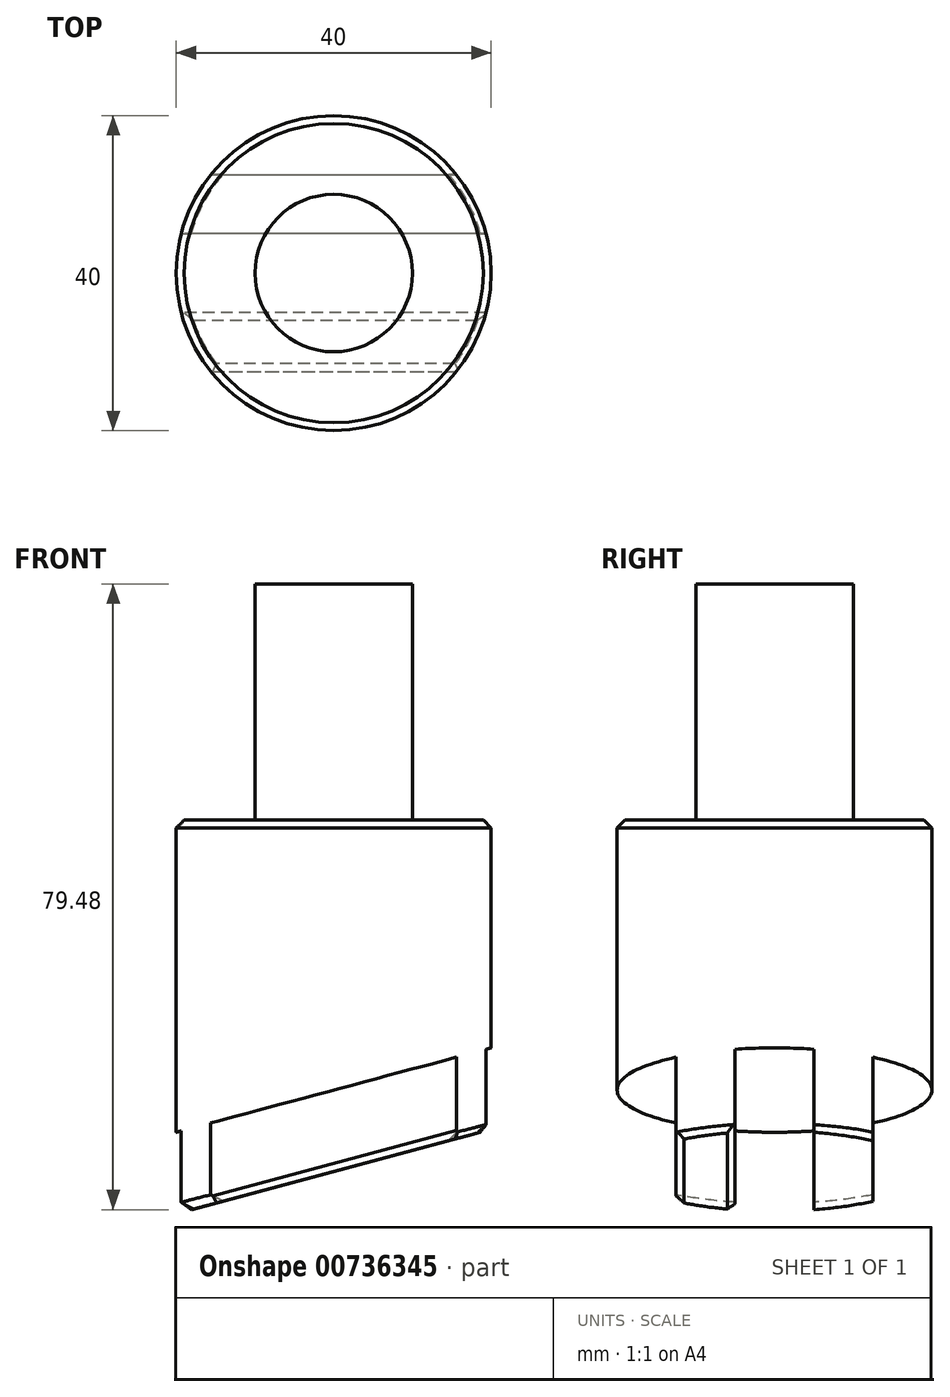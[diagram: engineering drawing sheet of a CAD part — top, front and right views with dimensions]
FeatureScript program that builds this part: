
annotation { "Feature Type Name" : "Feature", "Feature Type Description" : "" }
export const myFeature = defineFeature(function(context is Context, id is Id, definition is map)
    precondition{}
    {
        {
            var Q0;
            Q0=qCreatedBy(makeId("Front.planeOp"),FACE);
            var sketch = newSketch(context, id + "F0", { "sketchPlane" : qUnion([Q0])});
            skLineSegment(sketch, "E0", {"start": v(0, 0) * mm, "end": v(0, 80) * mm});
            skLineSegment(sketch, "E1", {"start": v(0, 80) * mm, "end": v(-10, 80) * mm});
            skLineSegment(sketch, "E2", {"start": v(-10, 80) * mm, "end": v(-10, 50) * mm});
            skLineSegment(sketch, "E3", {"start": v(-10, 50) * mm, "end": v(-20, 50) * mm});
            skLineSegment(sketch, "E4", {"start": v(-20, 50) * mm, "end": v(-20, 0) * mm});
            skLineSegment(sketch, "E5", {"start": v(-20, 0) * mm, "end": v(0, 0) * mm});
            skSolve(sketch);
        }
        {
            var Q0;
            Q0=makeQuery(id+"F0.imprint","IMPRINT",FACE,{"disambiguationData":[TD([[makeQuery(id+"F0.imprint","IMPRINT",EDGE,{"derivedFrom":sQuery(id+"F0.wireOp",EDGE,"E0")}),1.0]])]});
            var Q1;
            Q1=sQuery(id+"F0.wireOp",EDGE,"E0");
            revolve(context, id + "F1", {"surfaceOperationType" : NewSurfaceOperationType.NEW, "entities" : qUnion([Q0]), "axis" : qUnion([Q1]), "revolveType" : RevolveType.FULL});
        }
        {
            var Q0;
            Q0=qCreatedBy(makeId("Front.planeOp"),FACE);
            var sketch = newSketch(context, id + "F2", { "sketchPlane" : qUnion([Q0])});
            skLineSegment(sketch, "E6", {"start": v(-20, 0) * mm, "end": v(20, 10.72) * mm});
            skLineSegment(sketch, "E7", {"start": v(-20, 0) * mm, "end": v(20, 0) * mm});
            skLineSegment(sketch, "E8", {"start": v(20, 0) * mm, "end": v(20, 10.72) * mm});
            skSolve(sketch);
        }
        {
            var Q0;
            Q0 = qSketchRegion(id + "F2", true);
            extrude(context, id + "F3", {"entities" : qUnion([Q0]), "operationType" : NewBodyOperationType.REMOVE, "endBound" : BoundingType.SYMMETRIC, "depth" : 40 * mm, "offsetDistance" : 25 * mm});
        }
        {
            var Q0;
            Q0=makeQuery(id+"F3.boolean.opBoolean","COPY",FACE,{"derivedFrom":makeQuery(id+"F3.opExtrude","SWEPT_FACE",FACE,{"disambiguationData":[OSD([sQuery(id+"F2.wireOp",EDGE,"E6")])]})});
            var sketch = newSketch(context, id + "F4", { "sketchPlane" : qUnion([Q0])});
            skLineSegment(sketch, "E9.bottom", {"start": v(30, -5) * mm, "end": v(-30, -5) * mm});
            skLineSegment(sketch, "E9.top", {"start": v(30, 5) * mm, "end": v(-30, 5) * mm});
            skLineSegment(sketch, "E9.left", {"start": v(30, -5) * mm, "end": v(30, 5) * mm});
            skLineSegment(sketch, "E9.right", {"start": v(-30, -5) * mm, "end": v(-30, 5) * mm});
            skPoint(sketch, "E9.middle", {"position": v(0, 0) * mm});
            skLineSegment(sketch, "E10", {"start": v(-30, 12.5) * mm, "end": v(30, 12.5) * mm});
            skLineSegment(sketch, "E11", {"start": v(30, 12.5) * mm, "end": v(30, 25) * mm});
            skLineSegment(sketch, "E12", {"start": v(30, 25) * mm, "end": v(-30, 25) * mm});
            skLineSegment(sketch, "E13", {"start": v(-30, 25) * mm, "end": v(-30, 12.5) * mm});
            skLineSegment(sketch, "E14.MirrorCS", {"start": v(30, -12.5) * mm, "end": v(30, -25) * mm});
            skLineSegment(sketch, "E15.MirrorCS", {"start": v(30, -25) * mm, "end": v(-30, -25) * mm});
            skLineSegment(sketch, "E16.MirrorCS", {"start": v(-30, -12.5) * mm, "end": v(30, -12.5) * mm});
            skLineSegment(sketch, "E17.MirrorCS", {"start": v(-30, -25) * mm, "end": v(-30, -12.5) * mm});
            skSolve(sketch);
        }
        {
            var Q0;
            Q0 = qSketchRegion(id + "F4", true);
            extrude(context, id + "F5", {"entities" : qUnion([Q0]), "operationType" : NewBodyOperationType.REMOVE, "oppositeDirection" : true, "depth" : 10 * mm, "offsetDistance" : 25 * mm});
        }
        {
            var Q0;
            Q0=makeQuery(id+"F1.opRevolve","SWEPT_EDGE",EDGE,{"disambiguationData":[OSD([sQuery(id+"F0.wireOp",EDGE,"E3"),sQuery(id+"F0.wireOp",EDGE,"E4")])]});
            var Q1;
            Q1=makeQuery(id+"F3.boolean.opBoolean","INTERSECT",EDGE,{"derivedFrom":[makeQuery(id+"F1.opRevolve","SWEPT_FACE",FACE,{"disambiguationData":[OSD([sQuery(id+"F0.wireOp",EDGE,"E4")])]}),makeQuery(id+"F3.opExtrude","SWEPT_FACE",FACE,{"disambiguationData":[OSD([sQuery(id+"F2.wireOp",EDGE,"E6")])]})]});
            var Q2;
            Q2=makeQuery(id+"F5.boolean.opBoolean","COPY",EDGE,{"derivedFrom":makeQuery(id+"F5.opExtrude","CAP_EDGE",EDGE,{"disambiguationData":[OSD([sQuery(id+"F4.wireOp",EDGE,"E9.top")])],"isStart":true})});
            var Q3;
            Q3=makeQuery(id+"F5.boolean.opBoolean","COPY",EDGE,{"derivedFrom":makeQuery(id+"F5.opExtrude","CAP_EDGE",EDGE,{"disambiguationData":[OSD([sQuery(id+"F4.wireOp",EDGE,"E9.bottom")])],"isStart":true})});
            var Q4;
            Q4=makeQuery(id+"F5.boolean.opBoolean","COPY",EDGE,{"derivedFrom":makeQuery(id+"F5.opExtrude","CAP_EDGE",EDGE,{"disambiguationData":[OSD([sQuery(id+"F4.wireOp",EDGE,"E10")])],"isStart":true})});
            var Q5;
            Q5=makeQuery(id+"F5.boolean.opBoolean","COPY",EDGE,{"derivedFrom":makeQuery(id+"F5.opExtrude","CAP_EDGE",EDGE,{"disambiguationData":[OSD([sQuery(id+"F4.wireOp",EDGE,"E16.MirrorCS")])],"isStart":true})});
            chamfer(context, id + "F6", {"entities" : qUnion([Q0, Q1, Q2, Q3, Q4, Q5]), "width" : 1 * mm, "tangentPropagation" : true});
        }
    });
